# Revit family: bela_cliplamp
name_source: partatom
category: Luminarias
units: mm (PartAtom-declared; Revit-internal decimal feet)

## family parameters
Compartido = No
Corte con vacíos al cargar = Sí
Cota de conector redondo = Diámetro de uso
Número OmniClass = 23.80.70.00
Origen de luz = No
Punto de cálculo de habitación = No
Se basa en plano de trabajo = Sí
Siempre vertical = No
Tipo de pieza = Normal
Título OmniClass = Lighting

## types (4) — shared parameters
Elevación por defecto = 1219 mm
FARO_Category = Indoor
FARO_Last Actualization Date = 5/12/2024
FARO_Material_00 = Default Light Source
FARO_Material_02 = <Por categoría>
FARO_Model Line = BELA
FARO_Subcategory = CLIP
Fabricante = FARO Barcelona
Lámpara = 1 X E27 40W
URL = https://www.faro.es
Voltage = 100-240 V

## per-type parameters (varying)
| type | FARO_Description EN | FARO_Description ES | FARO_Material_01 | FARO_Ref |
| 56100 BELA Black clip lamp | BELA Black clip lamp | BELA Lámpara pinza negro | FARO_Black Paint | 56100 |
| 56101 BELA White clip lamp | BELA White clip lamp | BELA Lámpara pinza blanco | FARO_White shiny | 56101 |
| 56102 BELA Blue clip lamp | BELA Blue clip lamp | BELA Lámpara pinza azul | FARO_Blue | 56102 |
| 56103 BELA Red clip lamp | BELA Red clip lamp | BELA Lámpara pinza rojo | FARO_Red | 56103 |

## geometry (parser evidence)
native form markers: Sweep x7
no freeform markers — native parametric forms only
